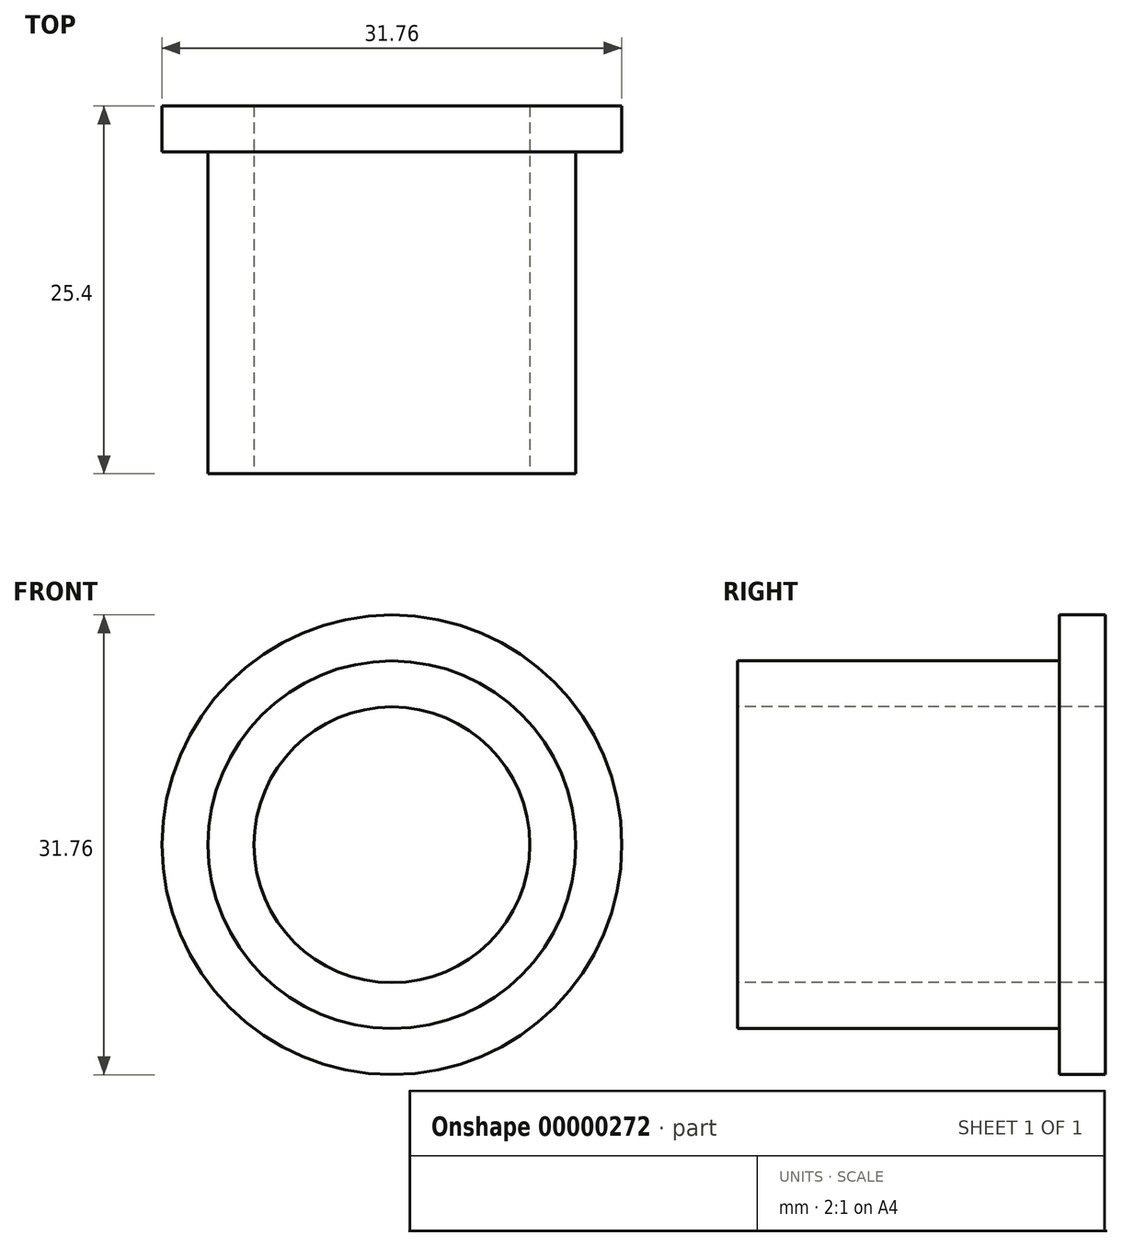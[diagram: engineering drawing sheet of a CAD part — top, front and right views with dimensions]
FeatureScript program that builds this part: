
annotation { "Feature Type Name" : "Feature", "Feature Type Description" : "" }
export const myFeature = defineFeature(function(context is Context, id is Id, definition is map)
    precondition{}
    {
        {
            var Q0;
            Q0=qCreatedBy(makeId("Front.planeOp"),FACE);
            var sketch = newSketch(context, id + "F0", { "sketchPlane" : qUnion([Q0])});
            skCircle(sketch, "E0", {"center": v(0, 0) * mm, "radius": 15.88 * mm});
            skSolve(sketch);
        }
        {
            var Q0;
            Q0=makeQuery(id+"F0.imprint","IMPRINT",FACE,{"disambiguationData":[TD([[makeQuery(id+"F0.imprint","IMPRINT",EDGE,{"derivedFrom":sQuery(id+"F0.wireOp",EDGE,"E0")}),1.0]])]});
            extrude(context, id + "F1", {"entities" : qUnion([Q0]), "depth" : 3.17 * mm});
        }
        {
            var Q0;
            Q0=makeQuery(id+"F1.opExtrude","CAP_FACE",FACE,{"disambiguationData":[OSD([sQuery(id+"F0.wireOp",EDGE,"E0")])],"isStart":false});
            var sketch = newSketch(context, id + "F2", { "sketchPlane" : qUnion([Q0])});
            skCircle(sketch, "E1", {"center": v(0, 0) * mm, "radius": 12.7 * mm});
            skSolve(sketch);
        }
        {
            var Q0;
            Q0=makeQuery(id+"F2.imprint","IMPRINT",FACE,{"disambiguationData":[TD([[makeQuery(id+"F2.imprint","IMPRINT",EDGE,{"derivedFrom":sQuery(id+"F2.wireOp",EDGE,"E1")}),1.0]])]});
            extrude(context, id + "F3", {"entities" : qUnion([Q0]), "operationType" : NewBodyOperationType.ADD, "depth" : 22.22 * mm});
        }
        {
            var Q0;
            Q0=makeQuery(id+"F3.opExtrude","CAP_FACE",FACE,{"disambiguationData":[OSD([sQuery(id+"F2.wireOp",EDGE,"E1")])],"isStart":false});
            var sketch = newSketch(context, id + "F4", { "sketchPlane" : qUnion([Q0])});
            skCircle(sketch, "E2", {"center": v(0, 0) * mm, "radius": 9.53 * mm});
            skSolve(sketch);
        }
        {
            var Q0;
            Q0=makeQuery(id+"F4.imprint","IMPRINT",FACE,{"disambiguationData":[TD([[makeQuery(id+"F4.imprint","IMPRINT",EDGE,{"derivedFrom":sQuery(id+"F4.wireOp",EDGE,"E2")}),1.0]])]});
            extrude(context, id + "F5", {"entities" : qUnion([Q0]), "operationType" : NewBodyOperationType.REMOVE, "endBound" : BoundingType.THROUGH_ALL, "oppositeDirection" : true, "depth" : 25.4 * mm});
        }
    });
